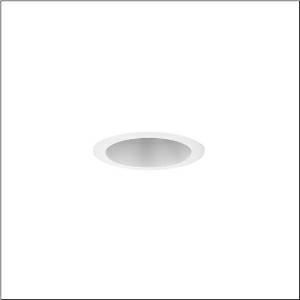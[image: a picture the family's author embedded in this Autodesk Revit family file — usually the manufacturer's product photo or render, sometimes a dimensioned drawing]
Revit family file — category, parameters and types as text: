
# Revit family: lunis_31_mini_51dn16de41
name_source: partatom
category: Lighting Fixtures
units: mm (PartAtom-declared; Revit-internal decimal feet)

## family parameters
Cut with Voids When Loaded = No
Host = Face
Light Source = No
Part Type = Normal
Room Calculation Point = No
Round Connector Dimension = Use Diameter
Shared = No

## types (1)
- Lunis 31 mini (1 x LED, 1040 lm, 8.3 W, 4000K)
    Apparent Load = 8 VA
    CIE Flux Codes = 69 93 99 100 100
    Color Rendering = 80
    Color Temperature = 4000K
    Default Elevation = 1800 mm
    Description = Lunis 31,  mini, downlight, light control with reflector, light emission: direct distribution, LED rated luminous flux: 1.040lm, light colour: 840, control gear: ECG DALI, mains connection: 220..240V, AC, 50/60Hz, housing, white, protection rating (complete): IP20, insulation class (complete): insulation class II (safety insulation), certification: CE, packaging unit: 1 piece
    Height = 0 mm  [stored 0 ft]
    Lamp = 1 x LED
    Lamp Light Flux = 1040 lm
    Lamp Power = 8.3 W
    Lamp count = 1
    Length = 188 mm  [stored 0.616798 ft]
    Luminous efficacy = 125 lm/W
    Manufacturer = Siteco
    ModVariant = No
    Model = 51DN16DE41
    Mounting Place = Ceiling
    Mounting Type = Recessed
    Number of Poles = 1
    OnlyDefault = Yes
    Power Factor = 1
    Product Name = Lunis 31 mini
    Product group = downlight | ceiling recessed
    ProductGroupID = 402
    Protection Class = Protection class II
    Protection Degree = IP 20
    RLX_Detail_Level = 1
    RlxData = <blob elided: 21689 chars, md5=14ae8be8>
    Socket = socket
    Standby Power = 0 W
    System Light Flux = 1040 lm
    System Power = 8 W
    Type Comments = Product without accessories
    Type Image = l_1005624.jpg
    URL = http://relux.com
    VarID = ---
    Voltage = 0 V
    Weight = 0.00 kg
    Width = 0 mm  [stored 0 ft]

note: [stored X ft] marks values corroborated as IEEE doubles in the binary element streams (Revit-internal decimal feet)

## geometry (parser evidence)
native form markers: Blend x4, Sweep x12
no freeform markers — native parametric forms only
